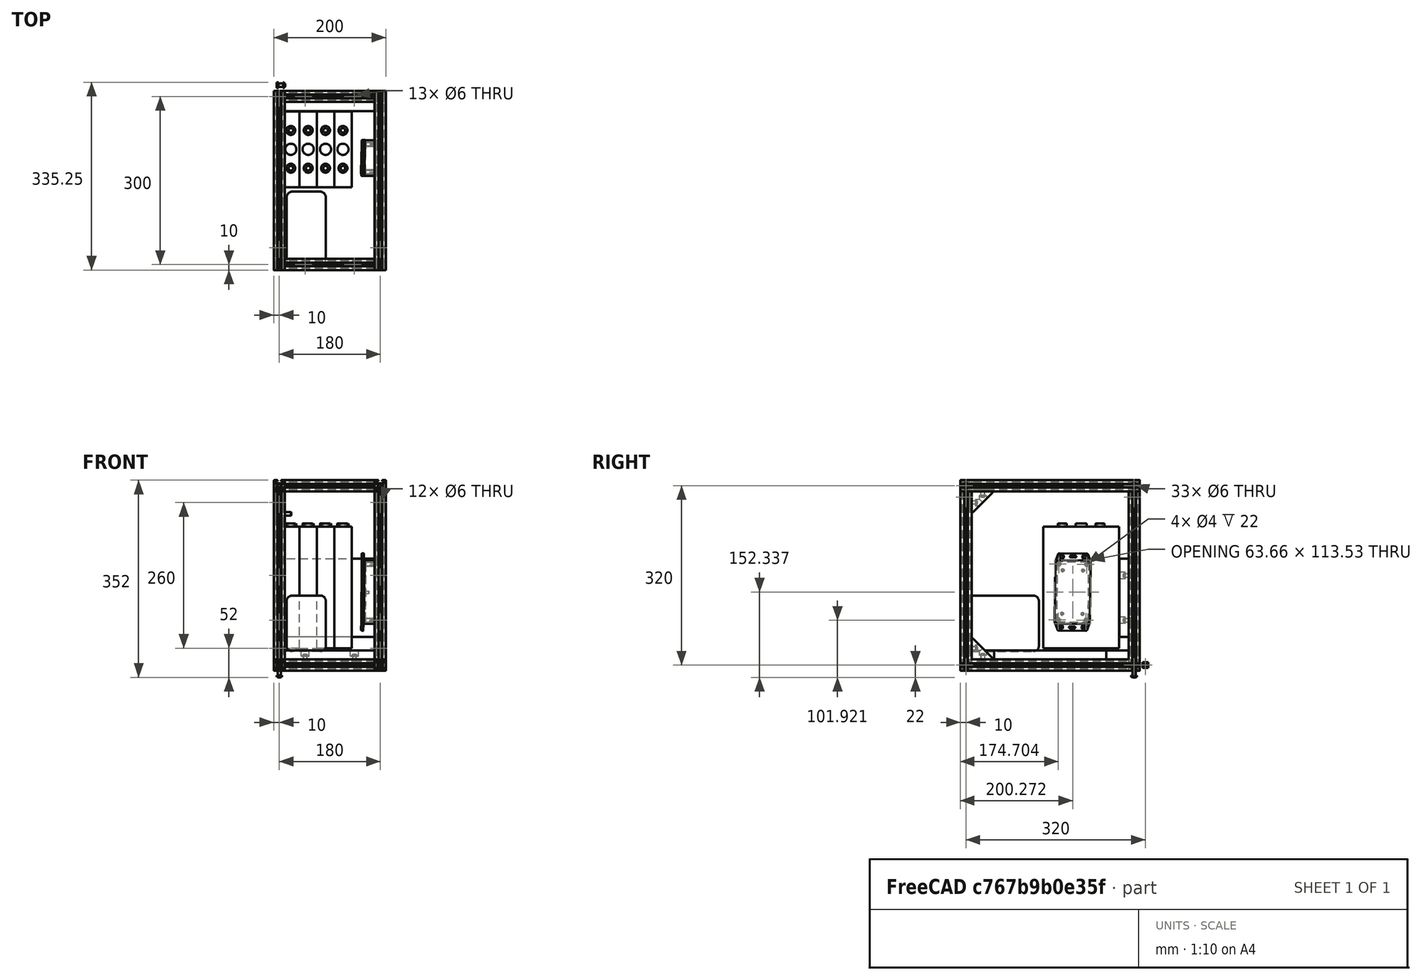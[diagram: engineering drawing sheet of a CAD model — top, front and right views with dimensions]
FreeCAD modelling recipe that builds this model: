
FCSTD DOCUMENT  (FreeCAD 0.16R6706 (Git))
Label: Solarbox_v_06_boxframe
License: All rights reserved
LicenseURL: http://en.wikipedia.org/wiki/All_rights_reserved
objects: Part::Feature×48, PartDesign::Fillet×32, PartDesign::Chamfer×24, Part::FeaturePython×13, Part::Compound×10, PartDesign::Pocket×9, App::FeaturePython×4, PartDesign::Body×1, Part::Box×1, Part::Fillet×1, Part::MultiFuse×1
note: 149 computed .brp shape members not serialized (recipe doc carries the construction recipe); baked Part::Feature solids carry a one-line shape summary decoded from their .brp

FEATURE [Part::Feature] Pocket003001  label="tslot32con"
  Placement = pos=(0,10,10) rot=(1,0,0;1.5708rad)
  shape: bbox 20 x 320 x 20 mm, 150 faces (baked)
FEATURE [Part::Feature] Pocket003002  label="tslot16"
  Placement = pos=(10,0,10) rot=(0,1,0;1.5708rad)
  shape: bbox 160 x 20 x 20 mm, 94 faces (baked)
FEATURE [Part::Feature] Pocket003006  label="tslot16_001"
  Placement = pos=(10,-300,10) rot=(0,1,0;1.5708rad)
  shape: bbox 160 x 20 x 20 mm, 94 faces (baked)
FEATURE [Part::Feature] Pocket003007  label="tslot32con_001"
  Placement = pos=(180,-310,10) rot=(0,0.707107,0.707107;3.14159rad)
  shape: bbox 20 x 320 x 20 mm, 150 faces (baked)
FEATURE [Part::FeaturePython] Screw  label="M6x25-Screw"  # Fasteners workbench fastener (typed FeaturePython)
  Placement = pos=(-4,0,10) rot=(0,-1,0;1.5708rad)
  diameter = 7
  invert = false
  length = 6
  matchOuter = false
  offset = 0
  thread = false
  type = 15
FEATURE [Part::FeaturePython] Screw001  label="M6x25-Screw004"  # Fasteners workbench fastener (typed FeaturePython)
  Placement = pos=(-4,-300,10) rot=(0,-1,0;1.5708rad)
  diameter = 7
  invert = false
  length = 6
  matchOuter = false
  offset = 0
  thread = false
  type = 15
FEATURE [Part::FeaturePython] Screw002  label="M6x25-Screw005"  # Fasteners workbench fastener (typed FeaturePython)
  Placement = pos=(184,0,10) rot=(0,1,0;1.5708rad)
  diameter = 7
  invert = false
  length = 6
  matchOuter = false
  offset = 0
  thread = false
  type = 15
FEATURE [Part::FeaturePython] Screw004  label="M6x25-Screw006"  # Fasteners workbench fastener (typed FeaturePython)
  Placement = pos=(184,-300,10) rot=(0,1,0;1.5708rad)
  diameter = 7
  invert = false
  length = 6
  matchOuter = false
  offset = 0
  thread = false
  type = 15
FEATURE [Part::Feature] Pocket003008  label="tslot32con001"
  Placement = pos=(0,10,330) rot=(1,0,0;1.5708rad)
  shape: bbox 20 x 320 x 20 mm, 150 faces (baked)
FEATURE [Part::Feature] Pocket003009  label="tslot041"
  Placement = pos=(10,0,330) rot=(0,1,0;1.5708rad)
  shape: bbox 160 x 20 x 20 mm, 94 faces (baked)
FEATURE [Part::Feature] Pocket003010  label="tslot16_002"
  Placement = pos=(10,-300,330) rot=(0,1,0;1.5708rad)
  shape: bbox 160 x 20 x 20 mm, 94 faces (baked)
FEATURE [Part::Feature] Pocket003011  label="tslot32con_002"
  Placement = pos=(180,-310,330) rot=(0,0.707107,0.707107;3.14159rad)
  shape: bbox 20 x 320 x 20 mm, 150 faces (baked)
FEATURE [Part::FeaturePython] Screw005  label="M6x25-Screw007"  # Fasteners workbench fastener (typed FeaturePython)
  Placement = pos=(-4,0,280) rot=(0,-1,0;1.5708rad)
  diameter = 7
  invert = false
  length = 6
  matchOuter = false
  offset = 0
  thread = false
  type = 15
FEATURE [Part::FeaturePython] Screw006  label="M6x25-Screw008"  # Fasteners workbench fastener (typed FeaturePython)
  Placement = pos=(-4,-300,330) rot=(0,-1,0;1.5708rad)
  diameter = 7
  invert = false
  length = 6
  matchOuter = false
  offset = 0
  thread = false
  type = 15
FEATURE [Part::FeaturePython] Screw007  label="M6x25-Screw009"  # Fasteners workbench fastener (typed FeaturePython)
  Placement = pos=(184,0,330) rot=(0,1,0;1.5708rad)
  diameter = 7
  invert = false
  length = 6
  matchOuter = false
  offset = 0
  thread = false
  type = 15
FEATURE [Part::FeaturePython] Screw008  label="M6x25-Screw010"  # Fasteners workbench fastener (typed FeaturePython)
  Placement = pos=(184,-300,330) rot=(0,1,0;1.5708rad)
  diameter = 7
  invert = false
  length = 6
  matchOuter = false
  offset = 0
  thread = false
  type = 15
FEATURE [Part::Feature] Body009001  label="m6nutplate010"
  Placement = pos=(-1.5,15,5) rot=(0,-1,0;1.5708rad)
  shape: bbox 3 x 10 x 10 mm, 9 faces (baked)
FEATURE [Part::Feature] Body010001  label="m6nutplate011"
  Placement = pos=(15,41.5,5) rot=(0.57735,0.57735,0.57735;4.18879rad)
  shape: bbox 10 x 3 x 10 mm, 9 faces (baked)
FEATURE [Part::Feature] Screw018001  label="M6x12-Screw010"
  Placement = pos=(20,33,10) rot=(1,0,0;1.5708rad)
  shape: bbox 10.5 x 15.3 x 10.5 mm, 15 faces (baked)
FEATURE [Part::Feature] Screw017001  label="M6x12-Screw011"
  Placement = pos=(7,20,10) rot=(0,1,0;1.5708rad)
  shape: bbox 15.3 x 10.5 x 10.5 mm, 15 faces (baked)
FEATURE [Part::Feature] Fillet004005001  label="Fillet004005037"
  shape: bbox 37.5 x 37.5 x 20 mm, 26 faces (baked)
FEATURE [Part::Compound] Compound
  Links = -> [Body009001,Fillet004005001,Screw017001,Body010001,Screw018001]
  Placement = pos=(10,-250,320) rot=(0.707107,0,-0.707107;3.14159rad)
FEATURE [Part::Feature] Body010002  label="m6nutplate012"
  Placement = pos=(-1.5,15,5) rot=(0,-1,0;1.5708rad)
  shape: bbox 3 x 10 x 10 mm, 9 faces (baked)
FEATURE [Part::Feature] Body010003  label="m6nutplate013"
  Placement = pos=(15,41.5,5) rot=(0.57735,0.57735,0.57735;4.18879rad)
  shape: bbox 10 x 3 x 10 mm, 9 faces (baked)
FEATURE [Part::Feature] Screw018002  label="M6x12-Screw012"
  Placement = pos=(20,33,10) rot=(1,0,0;1.5708rad)
  shape: bbox 10.5 x 15.3 x 10.5 mm, 15 faces (baked)
FEATURE [Part::Feature] Screw018003  label="M6x12-Screw013"
  Placement = pos=(7,20,10) rot=(0,1,0;1.5708rad)
  shape: bbox 15.3 x 10.5 x 10.5 mm, 15 faces (baked)
FEATURE [Part::Feature] Fillet004005002  label="Fillet011"
  shape: bbox 37.5 x 37.5 x 20 mm, 26 faces (baked)
FEATURE [Part::Compound] Compound001
  Links = -> [Body010002,Fillet004005002,Screw018003,Body010003,Screw018002]
  Placement = pos=(190,-250,320) rot=(0.707107,0,-0.707107;3.14159rad)
FEATURE [Part::Feature] Body010004  label="m6nutplate014"
  Placement = pos=(-1.5,15,5) rot=(0,-1,0;1.5708rad)
  shape: bbox 3 x 10 x 10 mm, 9 faces (baked)
FEATURE [Part::Feature] Body010005  label="m6nutplate015"
  Placement = pos=(15,41.5,5) rot=(0.57735,0.57735,0.57735;4.18879rad)
  shape: bbox 10 x 3 x 10 mm, 9 faces (baked)
FEATURE [Part::Feature] Screw018004  label="M6x12-Screw014"
  Placement = pos=(20,33,10) rot=(1,0,0;1.5708rad)
  shape: bbox 10.5 x 15.3 x 10.5 mm, 15 faces (baked)
FEATURE [Part::Feature] Screw018005  label="M6x12-Screw015"
  Placement = pos=(7,20,10) rot=(0,1,0;1.5708rad)
  shape: bbox 15.3 x 10.5 x 10.5 mm, 15 faces (baked)
FEATURE [Part::Feature] Fillet004005003  label="Fillet012"
  shape: bbox 37.5 x 37.5 x 20 mm, 26 faces (baked)
FEATURE [Part::Compound] Compound002
  Links = -> [Body010004,Fillet004005003,Screw018005,Body010005,Screw018004]
  Placement = pos=(10,-290,60) rot=(0.57735,0.57735,-0.57735;4.18879rad)
FEATURE [Part::Feature] Body010006  label="m6nutplate016"
  Placement = pos=(-1.5,15,5) rot=(0,-1,0;1.5708rad)
  shape: bbox 3 x 10 x 10 mm, 9 faces (baked)
FEATURE [Part::Feature] Body010007  label="m6nutplate017"
  Placement = pos=(15,41.5,5) rot=(0.57735,0.57735,0.57735;4.18879rad)
  shape: bbox 10 x 3 x 10 mm, 9 faces (baked)
FEATURE [Part::Feature] Screw018006  label="M6x12-Screw016"
  Placement = pos=(20,33,10) rot=(1,0,0;1.5708rad)
  shape: bbox 10.5 x 15.3 x 10.5 mm, 15 faces (baked)
FEATURE [Part::Feature] Screw018007  label="M6x12-Screw017"
  Placement = pos=(7,20,10) rot=(0,1,0;1.5708rad)
  shape: bbox 15.3 x 10.5 x 10.5 mm, 15 faces (baked)
FEATURE [Part::Feature] Fillet004005004  label="Fillet013"
  shape: bbox 37.5 x 37.5 x 20 mm, 26 faces (baked)
FEATURE [Part::Compound] Compound003
  Links = -> [Body010006,Fillet004005004,Screw018007,Body010007,Screw018006]
  Placement = pos=(190,-290,60) rot=(0.57735,0.57735,-0.57735;4.18879rad)
FEATURE [Part::FeaturePython] Screw018016  label="M6x12-Screw026"  # Fasteners workbench fastener (typed FeaturePython)
  diameter = 4
  invert = false
  length = 1
  matchOuter = false
  offset = 0
  thread = false
  type = 20
FEATURE [Part::Feature] Body010016  label="m6nutplate026"
  Placement = pos=(5,-5,-8.39) rot=(0,1,0;3.14159rad)
  shape: bbox 10 x 10 x 3 mm, 9 faces (baked)
FEATURE [Part::Compound] Compound016  label="bottom_plate"
  Placement = pos=(190,-310,20) rot=(0,0,1;1.5708rad)
FEATURE [Part::Feature] Body010023  label="cam72calb3"
  Placement = pos=(5,-162,40) rot=(0,0,1;0rad)
  shape: bbox 31 x 135.1 x 222.5 mm, 16 faces (baked)
FEATURE [Part::Feature] Body010024  label="cam72calb004"
  Placement = pos=(36,-162,40) rot=(0,0,1;0rad)
  shape: bbox 31 x 135.1 x 222.5 mm, 16 faces (baked)
FEATURE [Part::Feature] Body010025  label="cam72calb005"
  Placement = pos=(67,-162,40) rot=(0,0,1;0rad)
  shape: bbox 31 x 135.1 x 222.5 mm, 16 faces (baked)
FEATURE [Part::Feature] Body010026  label="cam72calb006"
  Placement = pos=(98,-162,40) rot=(0,0,1;0rad)
  shape: bbox 31 x 135.1 x 222.5 mm, 16 faces (baked)
FEATURE [PartDesign::Body] Body010027
FEATURE [PartDesign::Pocket] Pocket003019
  Length = 10
  Placement = pos=(130,-166,235) rot=(0,1,0;1.5708rad)
  Type = 0
FEATURE [Part::FeaturePython] Screw018021  label="M6x12-Screw032"  # Fasteners workbench fastener (typed FeaturePython)
  diameter = 4
  invert = false
  length = 1
  matchOuter = false
  offset = 0
  thread = false
  type = 20
FEATURE [Part::Feature] Body010028  label="m6nutplate032"
  Placement = pos=(5,-5,-8.39) rot=(0,1,0;3.14159rad)
  shape: bbox 10 x 10 x 3 mm, 9 faces (baked)
FEATURE [App::FeaturePython] circularEdgeConstraint009  # a2plus constraint (typed FeaturePython)
  Object1 = Screw
  Object2 = Body001
  SubElement1 = Edge7
  SubElement2 = Edge20
  Type = circularEdge
  directionConstraint = 1
  lockRotation = false
  offset = 0
FEATURE [Part::Compound] Compound017  label="nutplate12screw008"
  Links = -> [Screw018021,circularEdgeConstraint009,Body010028]
  Placement = pos=(10,30,6) rot=(0,0,1;0rad)
FEATURE [Part::FeaturePython] Screw018022  label="M6x12-Screw033"  # Fasteners workbench fastener (typed FeaturePython)
  diameter = 4
  invert = false
  length = 1
  matchOuter = false
  offset = 0
  thread = false
  type = 20
FEATURE [Part::Feature] Body010029  label="m6nutplate033"
  Placement = pos=(5,-5,-8.39) rot=(0,1,0;3.14159rad)
  shape: bbox 10 x 10 x 3 mm, 9 faces (baked)
FEATURE [App::FeaturePython] circularEdgeConstraint010  # a2plus constraint (typed FeaturePython)
  Object1 = Screw
  Object2 = Body001
  SubElement1 = Edge7
  SubElement2 = Edge20
  Type = circularEdge
  directionConstraint = 1
  lockRotation = false
  offset = 0
FEATURE [Part::Compound] Compound018  label="nutplate12screw009"
  Links = -> [Screw018022,circularEdgeConstraint010,Body010029]
  Placement = pos=(10,110,6) rot=(0,0,1;0rad)
FEATURE [Part::FeaturePython] Screw018023  label="M6x12-Screw034"  # Fasteners workbench fastener (typed FeaturePython)
  diameter = 4
  invert = false
  length = 1
  matchOuter = false
  offset = 0
  thread = false
  type = 20
FEATURE [Part::Feature] Body010030  label="m6nutplate034"
  Placement = pos=(5,-5,-8.39) rot=(0,1,0;3.14159rad)
  shape: bbox 10 x 10 x 3 mm, 9 faces (baked)
FEATURE [App::FeaturePython] circularEdgeConstraint011  # a2plus constraint (typed FeaturePython)
  Object1 = Screw
  Object2 = Body001
  SubElement1 = Edge7
  SubElement2 = Edge20
  Type = circularEdge
  directionConstraint = 1
  lockRotation = false
  offset = 0
FEATURE [Part::Compound] Compound019  label="nutplate12screw010"
  Links = -> [Screw018023,circularEdgeConstraint011,Body010030]
  Placement = pos=(190,110,6) rot=(0,0,1;0rad)
FEATURE [Part::FeaturePython] Screw018024  label="M6x12-Screw035"  # Fasteners workbench fastener (typed FeaturePython)
  diameter = 4
  invert = false
  length = 1
  matchOuter = false
  offset = 0
  thread = false
  type = 20
FEATURE [Part::Feature] Body010031  label="m6nutplate035"
  Placement = pos=(5,-5,-8.39) rot=(0,1,0;3.14159rad)
  shape: bbox 10 x 10 x 3 mm, 9 faces (baked)
FEATURE [App::FeaturePython] circularEdgeConstraint012  # a2plus constraint (typed FeaturePython)
  Object1 = Screw
  Object2 = Body001
  SubElement1 = Edge7
  SubElement2 = Edge20
  Type = circularEdge
  directionConstraint = 1
  lockRotation = false
  offset = 0
FEATURE [Part::Compound] Compound020  label="nutplate12screw011"
  Links = -> [Screw018024,circularEdgeConstraint012,Body010031]
  Placement = pos=(190,30,6) rot=(0,0,1;0rad)
FEATURE [Part::Compound] Compound021  label="front_plate"
  Links = -> [Body010027,Compound020,Compound019,Compound017,Compound018]
  Placement = pos=(-10,-10,60) rot=(1,0,0;1.5708rad)
FEATURE [Part::Box] Box003  label="MPPT"
  Height = 100
  Length = 130
  Placement = pos=(290,128,10) rot=(0,0,1;0rad)
  Width = 70
FEATURE [Part::Fillet] Fillet007  label="MPPT               "
  Base = -> Box003
  Edges = 12 edges r=10: [Edge1,Edge2,Edge3,Edge4,Edge5,Edge6,Edge7,Edge8,Edge9,Edge10,Edge11,Edge12]
  Placement = pos=(211,-590,24) rot=(0,0,1;1.5708rad)
FEATURE [Part::Feature] Part__Feature1213002  label="1591XXBF LID002"
  Placement = pos=(-49.5922,26.5,21.832) rot=(-0.57735,0.57735,0.57735;2.0944rad)
  shape: bbox 138 x 12.61 x 63.32 mm, 220 faces (baked)
FEATURE [Part::Feature] Part__Feature1213003  label="1591XXB BOX002"
  Placement = pos=(0,0,0) rot=(0,0.707107,0.707107;3.14159rad)
  shape: bbox 113.8 x 28.25 x 63.32 mm, 133 faces (baked)
FEATURE [Part::MultiFuse] Fusion002  label="FusionCover"
  Placement = pos=(177.976,-110.123,140.125) rot=(0.575193,-0.579099,0.577752;2.07392rad)
  Shapes = -> [Part__Feature1213002,Part__Feature1213003]
FEATURE [PartDesign::Pocket] Pocket015
  Length = 2
  Placement = pos=(-21,-320,-11) rot=(0,0,1;0rad)
  Type = 0
FEATURE [PartDesign::Fillet] Fillet
  Base = -> Pocket015 [Edge4,Edge5,Edge25]
  Placement = pos=(-21,-320,-11) rot=(0,0,1;0rad)
  Radius = 12
FEATURE [PartDesign::Fillet] Fillet001
  Base = -> Fillet [Edge75,Edge33,Edge61]
  Placement = pos=(-21,-320,-11) rot=(0,0,1;0rad)
  Radius = 6
FEATURE [PartDesign::Fillet] Fillet002
  Base = -> Fillet001 [Edge5,Edge16,Edge20]
  Placement = pos=(-21,-320,-11) rot=(0,0,1;0rad)
  Radius = 6
FEATURE [PartDesign::Fillet] Fillet003
  Base = -> Fillet002 [Edge34,Edge71,Edge47]
  Placement = pos=(-21,-320,-11) rot=(0,0,1;0rad)
  Radius = 6
FEATURE [PartDesign::Chamfer] Chamfer
  Base = -> Fillet003 [Edge45]
  Placement = pos=(-21,-320,-11) rot=(0,0,1;0rad)
  Size = 2
FEATURE [PartDesign::Chamfer] Chamfer001
  Base = -> Chamfer [Edge58]
  Placement = pos=(-21,-320,-11) rot=(0,0,1;0rad)
  Size = 2
FEATURE [PartDesign::Chamfer] Chamfer002
  Base = -> Chamfer001 [Edge159]
  Placement = pos=(-21,-320,-11) rot=(0,0,1;0rad)
  Size = 2
FEATURE [PartDesign::Pocket] Pocket003020
  Length = 2
  Placement = pos=(201,-320,-11) rot=(0,0,1;1.5708rad)
  Type = 0
FEATURE [PartDesign::Fillet] Fillet004005008  label="Fillet004005038"
  Base = -> Pocket003020 [Edge4,Edge5,Edge25]
  Placement = pos=(201,-320,-11) rot=(0,0,1;1.5708rad)
  Radius = 12
FEATURE [PartDesign::Fillet] Fillet004005009
  Base = -> Fillet004005008 [Edge75,Edge33,Edge61]
  Placement = pos=(201,-320,-11) rot=(0,0,1;1.5708rad)
  Radius = 6
FEATURE [PartDesign::Fillet] Fillet004005010
  Base = -> Fillet004005009 [Edge5,Edge16,Edge20]
  Placement = pos=(201,-320,-11) rot=(0,0,1;1.5708rad)
  Radius = 6
FEATURE [PartDesign::Fillet] Fillet004005011
  Base = -> Fillet004005010 [Edge34,Edge71,Edge47]
  Placement = pos=(201,-320,-11) rot=(0,0,1;1.5708rad)
  Radius = 6
FEATURE [PartDesign::Chamfer] Chamfer003
  Base = -> Fillet004005011 [Edge45]
  Placement = pos=(201,-320,-11) rot=(0,0,1;1.5708rad)
  Size = 2
FEATURE [PartDesign::Chamfer] Chamfer004
  Base = -> Chamfer003 [Edge58]
  Placement = pos=(201,-320,-11) rot=(0,0,1;1.5708rad)
  Size = 2
FEATURE [PartDesign::Chamfer] Chamfer005
  Base = -> Chamfer004 [Edge159]
  Placement = pos=(201,-320,-11) rot=(0,0,1;1.5708rad)
  Size = 2
FEATURE [PartDesign::Pocket] Pocket003021
  Length = 2
  Placement = pos=(-21,20,-11) rot=(1,0,0;1.5708rad)
  Type = 0
FEATURE [PartDesign::Fillet] Fillet004005012
  Base = -> Pocket003021 [Edge4,Edge5,Edge25]
  Placement = pos=(-21,20,-11) rot=(1,0,0;1.5708rad)
  Radius = 12
FEATURE [PartDesign::Fillet] Fillet004005013  label="Fillet004005039"
  Base = -> Fillet004005012 [Edge75,Edge33,Edge61]
  Placement = pos=(-21,20,-11) rot=(1,0,0;1.5708rad)
  Radius = 6
FEATURE [PartDesign::Fillet] Fillet004005014
  Base = -> Fillet004005013 [Edge5,Edge16,Edge20]
  Placement = pos=(-21,20,-11) rot=(1,0,0;1.5708rad)
  Radius = 6
FEATURE [PartDesign::Fillet] Fillet004005015
  Base = -> Fillet004005014 [Edge34,Edge71,Edge47]
  Placement = pos=(-21,20,-11) rot=(1,0,0;1.5708rad)
  Radius = 6
FEATURE [PartDesign::Chamfer] Chamfer006
  Base = -> Fillet004005015 [Edge45]
  Placement = pos=(-21,20,-11) rot=(1,0,0;1.5708rad)
  Size = 2
FEATURE [PartDesign::Chamfer] Chamfer007
  Base = -> Chamfer006 [Edge58]
  Placement = pos=(-21,20,-11) rot=(1,0,0;1.5708rad)
  Size = 2
FEATURE [PartDesign::Chamfer] Chamfer008
  Base = -> Chamfer007 [Edge159]
  Placement = pos=(-21,20,-11) rot=(1,0,0;1.5708rad)
  Size = 2
FEATURE [PartDesign::Pocket] Pocket003022
  Length = 2
  Placement = pos=(201,21,-10) rot=(0,0,1;3.14159rad)
  Type = 0
FEATURE [PartDesign::Fillet] Fillet004005016
  Base = -> Pocket003022 [Edge4,Edge5,Edge25]
  Placement = pos=(201,21,-10) rot=(0,0,1;3.14159rad)
  Radius = 12
FEATURE [PartDesign::Fillet] Fillet004005017  label="Fillet004005040"
  Base = -> Fillet004005016 [Edge75,Edge33,Edge61]
  Placement = pos=(201,21,-10) rot=(0,0,1;3.14159rad)
  Radius = 6
FEATURE [PartDesign::Fillet] Fillet004005018
  Base = -> Fillet004005017 [Edge5,Edge16,Edge20]
  Placement = pos=(201,21,-10) rot=(0,0,1;3.14159rad)
  Radius = 6
FEATURE [PartDesign::Fillet] Fillet004005019
  Base = -> Fillet004005018 [Edge34,Edge71,Edge47]
  Placement = pos=(201,21,-10) rot=(0,0,1;3.14159rad)
  Radius = 6
FEATURE [PartDesign::Chamfer] Chamfer009
  Base = -> Fillet004005019 [Edge45]
  Placement = pos=(201,21,-10) rot=(0,0,1;3.14159rad)
  Size = 2
FEATURE [PartDesign::Chamfer] Chamfer010
  Base = -> Chamfer009 [Edge58]
  Placement = pos=(201,21,-10) rot=(0,0,1;3.14159rad)
  Size = 2
FEATURE [PartDesign::Chamfer] Chamfer011
  Base = -> Chamfer010 [Edge159]
  Placement = pos=(201,21,-10) rot=(0,0,1;3.14159rad)
  Size = 2
FEATURE [PartDesign::Pocket] Pocket003023
  Length = 2
  Placement = pos=(-21,21,351) rot=(1,0,0;3.14159rad)
  Type = 0
FEATURE [PartDesign::Fillet] Fillet004005021  label="Fillet004005042"
  Base = -> Pocket003023 [Edge4,Edge5,Edge25]
  Placement = pos=(-21,21,351) rot=(1,0,0;3.14159rad)
  Radius = 12
FEATURE [PartDesign::Fillet] Fillet004005022  label="Fillet004005043"
  Base = -> Fillet004005021 [Edge75,Edge33,Edge61]
  Placement = pos=(-21,21,351) rot=(1,0,0;3.14159rad)
  Radius = 6
FEATURE [PartDesign::Fillet] Fillet004005023  label="Fillet004005044"
  Base = -> Fillet004005022 [Edge5,Edge16,Edge20]
  Placement = pos=(-21,21,351) rot=(1,0,0;3.14159rad)
  Radius = 6
FEATURE [PartDesign::Fillet] Fillet004005024  label="Fillet004005045"
  Base = -> Fillet004005023 [Edge34,Edge71,Edge47]
  Placement = pos=(-21,21,351) rot=(1,0,0;3.14159rad)
  Radius = 6
FEATURE [PartDesign::Chamfer] Chamfer012
  Base = -> Fillet004005024 [Edge45]
  Placement = pos=(-21,21,351) rot=(1,0,0;3.14159rad)
  Size = 2
FEATURE [PartDesign::Chamfer] Chamfer013
  Base = -> Chamfer012 [Edge58]
  Placement = pos=(-21,21,351) rot=(1,0,0;3.14159rad)
  Size = 2
FEATURE [PartDesign::Chamfer] Chamfer014
  Base = -> Chamfer013 [Edge159]
  Placement = pos=(-21,21,351) rot=(1,0,0;3.14159rad)
  Size = 2
FEATURE [PartDesign::Pocket] Pocket003024
  Length = 2
  Placement = pos=(201,-321,351) rot=(0,1,0;3.14159rad)
  Type = 0
FEATURE [PartDesign::Fillet] Fillet004005025
  Base = -> Pocket003024 [Edge4,Edge5,Edge25]
  Placement = pos=(201,-321,351) rot=(0,1,0;3.14159rad)
  Radius = 12
FEATURE [PartDesign::Fillet] Fillet004005026  label="Fillet004005046"
  Base = -> Fillet004005025 [Edge75,Edge33,Edge61]
  Placement = pos=(201,-321,351) rot=(0,1,0;3.14159rad)
  Radius = 6
FEATURE [PartDesign::Fillet] Fillet004005027
  Base = -> Fillet004005026 [Edge5,Edge16,Edge20]
  Placement = pos=(201,-321,351) rot=(0,1,0;3.14159rad)
  Radius = 6
FEATURE [PartDesign::Fillet] Fillet004005028
  Base = -> Fillet004005027 [Edge34,Edge71,Edge47]
  Placement = pos=(201,-321,351) rot=(0,1,0;3.14159rad)
  Radius = 6
FEATURE [PartDesign::Chamfer] Chamfer015
  Base = -> Fillet004005028 [Edge45]
  Placement = pos=(201,-321,351) rot=(0,1,0;3.14159rad)
  Size = 2
FEATURE [PartDesign::Chamfer] Chamfer016
  Base = -> Chamfer015 [Edge58]
  Placement = pos=(201,-321,351) rot=(0,1,0;3.14159rad)
  Size = 2
FEATURE [PartDesign::Chamfer] Chamfer017
  Base = -> Chamfer016 [Edge159]
  Placement = pos=(201,-321,351) rot=(0,1,0;3.14159rad)
  Size = 2
FEATURE [PartDesign::Pocket] Pocket003025
  Length = 2
  Placement = pos=(-21,-320,351) rot=(0,1,0;1.5708rad)
  Type = 0
FEATURE [PartDesign::Fillet] Fillet004005029  label="Fillet004005047"
  Base = -> Pocket003025 [Edge4,Edge5,Edge25]
  Placement = pos=(-21,-320,351) rot=(0,1,0;1.5708rad)
  Radius = 12
FEATURE [PartDesign::Fillet] Fillet004005030  label="Fillet004005048"
  Base = -> Fillet004005029 [Edge75,Edge33,Edge61]
  Placement = pos=(-21,-320,351) rot=(0,1,0;1.5708rad)
  Radius = 6
FEATURE [PartDesign::Fillet] Fillet004005031  label="Fillet004005049"
  Base = -> Fillet004005030 [Edge5,Edge16,Edge20]
  Placement = pos=(-21,-320,351) rot=(0,1,0;1.5708rad)
  Radius = 6
FEATURE [PartDesign::Fillet] Fillet004005032  label="Fillet004005050"
  Base = -> Fillet004005031 [Edge34,Edge71,Edge47]
  Placement = pos=(-21,-320,351) rot=(0,1,0;1.5708rad)
  Radius = 6
FEATURE [PartDesign::Chamfer] Chamfer018
  Base = -> Fillet004005032 [Edge45]
  Placement = pos=(-21,-320,351) rot=(0,1,0;1.5708rad)
  Size = 2
FEATURE [PartDesign::Chamfer] Chamfer019
  Base = -> Chamfer018 [Edge58]
  Placement = pos=(-21,-320,351) rot=(0,1,0;1.5708rad)
  Size = 2
FEATURE [PartDesign::Chamfer] Chamfer020
  Base = -> Chamfer019 [Edge159]
  Placement = pos=(-21,-320,351) rot=(0,1,0;1.5708rad)
  Size = 2
FEATURE [PartDesign::Pocket] Pocket003026
  Length = 2
  Placement = pos=(201,20,351) rot=(0.707107,-0.707107,0;3.14159rad)
  Type = 0
FEATURE [PartDesign::Fillet] Fillet004005033  label="Fillet004005051"
  Base = -> Pocket003026 [Edge4,Edge5,Edge25]
  Placement = pos=(201,20,351) rot=(0.707107,-0.707107,0;3.14159rad)
  Radius = 12
FEATURE [PartDesign::Fillet] Fillet004005034  label="Fillet004005052"
  Base = -> Fillet004005033 [Edge75,Edge33,Edge61]
  Placement = pos=(201,20,351) rot=(0.707107,-0.707107,0;3.14159rad)
  Radius = 6
FEATURE [PartDesign::Fillet] Fillet004005035  label="Fillet004005053"
  Base = -> Fillet004005034 [Edge5,Edge16,Edge20]
  Placement = pos=(201,20,351) rot=(0.707107,-0.707107,0;3.14159rad)
  Radius = 6
FEATURE [PartDesign::Fillet] Fillet004005036  label="Fillet004005054"
  Base = -> Fillet004005035 [Edge34,Edge71,Edge47]
  Placement = pos=(201,20,351) rot=(0.707107,-0.707107,0;3.14159rad)
  Radius = 6
FEATURE [PartDesign::Chamfer] Chamfer021
  Base = -> Fillet004005036 [Edge45]
  Placement = pos=(201,20,351) rot=(0.707107,-0.707107,0;3.14159rad)
  Size = 2
FEATURE [PartDesign::Chamfer] Chamfer022
  Base = -> Chamfer021 [Edge58]
  Placement = pos=(201,20,351) rot=(0.707107,-0.707107,0;3.14159rad)
  Size = 2
FEATURE [PartDesign::Chamfer] Chamfer023
  Base = -> Chamfer022 [Edge159]
  Placement = pos=(201,20,351) rot=(0.707107,-0.707107,0;3.14159rad)
  Size = 2
FEATURE [Part::Feature] Screw018013  label="M6x12-Screw023"
  Placement = pos=(7,20,10) rot=(0,1,0;1.5708rad)
  shape: bbox 15.3 x 10.5 x 10.5 mm, 15 faces (baked)
FEATURE [Part::Feature] Body010012  label="m6nutplate022"
  Placement = pos=(-1.5,15,5) rot=(0,-1,0;1.5708rad)
  shape: bbox 3 x 10 x 10 mm, 9 faces (baked)
FEATURE [Part::Feature] Screw018011  label="M6x12-Screw021"
  Placement = pos=(7,20,10) rot=(0,1,0;1.5708rad)
  shape: bbox 15.3 x 10.5 x 10.5 mm, 15 faces (baked)
FEATURE [Part::Feature] Body010008  label="m6nutplate018"
  Placement = pos=(-1.5,15,5) rot=(0,-1,0;1.5708rad)
  shape: bbox 3 x 10 x 10 mm, 9 faces (baked)
FEATURE [Part::Feature] Body010010  label="m6nutplate020"
  Placement = pos=(-1.5,15,5) rot=(0,-1,0;1.5708rad)
  shape: bbox 3 x 10 x 10 mm, 9 faces (baked)
FEATURE [Part::Feature] Pocket003027  label="tslot32con_003"
  Placement = pos=(180,-300,0) rot=(0,0,1;0rad)
  shape: bbox 20 x 20 x 320 mm, 150 faces (baked)
FEATURE [Part::Feature] Pocket003028  label="tslot32con_004"
  Placement = pos=(180,0,0) rot=(0,0,1;0rad)
  shape: bbox 20 x 20 x 320 mm, 150 faces (baked)
FEATURE [Part::Feature] Pocket003029  label="tslot32con_005"
  Placement = pos=(0,-300,0) rot=(0,0,1;0rad)
  shape: bbox 20 x 20 x 320 mm, 150 faces (baked)
FEATURE [Part::Feature] Pocket003030  label="tslot32con_006"
  shape: bbox 20 x 20 x 320 mm, 150 faces (baked)
